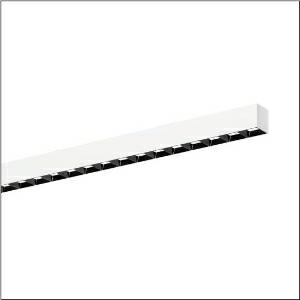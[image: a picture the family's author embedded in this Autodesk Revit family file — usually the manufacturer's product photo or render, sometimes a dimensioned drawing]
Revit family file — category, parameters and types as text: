
# Revit family: silica_21_51mx22da34wb
name_source: partatom
category: Lighting Fixtures
units: mm (PartAtom-declared; Revit-internal decimal feet)

## family parameters
Cut with Voids When Loaded = No
Host = Face
Light Source = No
Part Type = Normal
Room Calculation Point = No
Round Connector Dimension = Use Diameter
Shared = No

## types (1)
- --- (1 x LED, 4320 lm, 27.4 W, 3000K)
    Apparent Load = 27 VA
    CIE Flux Codes = 86 100 100 100 100
    Color Rendering = 80
    Color Temperature = 3000K
    Default Elevation = 1800 mm
    Description = Silica 21, office luminaire, primary light control with darklight reflector, of PMMA, black, CAT 2 (L<= 3000cd/m²), light emission: direct distribution, primary light characteristic: symmetric, installation type: surface-mounted, LED, rated luminous flux: 4.320lm, luminous efficacy: 158lm/W, light colour: 830, colour temperature: 3000K, control gear: DALI 2, with terminal, 3+2-pole, max. 2.5mm², mains connection: 220..240V, AC, 50/60Hz, rated input power: 27.4W, luminaire housing, of aluminium, traffic white (RAL 9016), length: 1.204mm, width: 53mm, height: 53mm, protection rating (complete): IP20, insulation class (complete): insulation class I (protective earthing), certification: CE, permissible operating ambient temperature: 0..+35°C, standard: EN 50419, packaging unit: 1 piece
    Height = 53 mm
    Lamp = 1 x LED
    Lamp Light Flux = 4320 lm
    Lamp Power = 27.4 W
    Lamp count = 1
    Length = 1204 mm
    Luminous efficacy = 158 lm/W
    Manufacturer = Siteco
    ModVariant = No
    Model = 51MX22DA34WB
    Mounting Place = Ceiling
    Mounting Type = Surface mounted
    Number of Poles = 1
    OnlyDefault = Yes
    Power Factor = 1
    Product Name = Silica 21
    Product group = office luminaire | ceiling mounted
    ProductGroupID = 301
    Protection Class = Protection class I
    Protection Degree = IP 20
    RLX_Detail_Level = 1
    RLX_Emergency_Light_Flux = 0 lm
    RLX_Emergency_Type = 0
    RLX_Emergency_Type_DB = No
    RlxData = <blob elided: 41245 chars, md5=66e2089a>
    Socket = socket
    Standby Power = 0 W
    System Light Flux = 4320 lm
    System Power = 27 W
    Type Comments = factory setting: luminous flux: 100 % | dim-lin: 254 | 392 mA
    Type Image = l_1335873.jpg
    URL = http://relux.com
    VarID = @adj_029085
    Voltage = 0 V
    Weight = 0.00 kg
    Width = 53 mm

## geometry (parser evidence)
native form markers: Blend x4, Sweep x11
no freeform markers — native parametric forms only
